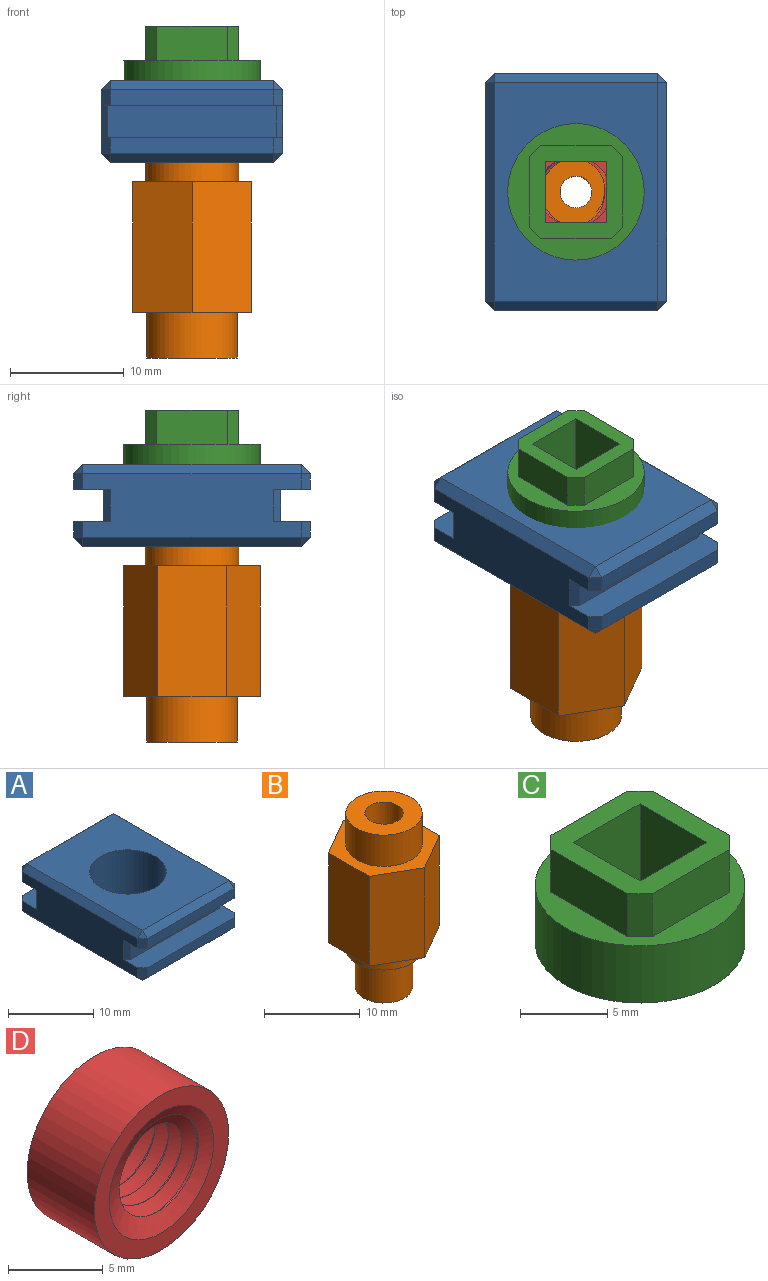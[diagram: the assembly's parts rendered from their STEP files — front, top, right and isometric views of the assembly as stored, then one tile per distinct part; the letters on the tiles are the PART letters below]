
ASSEMBLY  parts=4 mates=3
PART A: 43 faces, bbox 16x20.8x7.2 mm
  f0: plane 14.4x1.4mm, normal (0,-1,0), area 20.2mm2, adj f13,f31,f32,f33
  f1: plane 14.4x1.4mm, normal (0,1,0), area 20.2mm2, adj f11,f36,f39,f42
  f2: plane 19.2x5.6mm, normal (-1,0,0), area 94.1mm2, adj f9,f11,f12,f13,f15,f19,f20,f27
  f3: plane 19.2x5.6mm, normal (1,0,0), area 94.1mm2, adj f9,f11,f12,f13,f17,f23,f26,f29
  f4: plane 14.4x1.4mm, normal (0,-1,0), area 20.2mm2, adj f12,f15,f17,f18
  f5: cylinder r=4.5mm len=9mm, axis (0,0,-1), area 203.6mm2, adj f7,f8
  f6: plane 14.4x1.4mm, normal (0,1,0), area 20.2mm2, adj f9,f20,f24,f26
  f7: plane 19.2x14.4mm, normal (0,0,1), area 212.9mm2, adj f5,f18,f19,f23,f24
  f8: plane 19.2x14.4mm, normal (0,0,-1), area 212.9mm2, adj f5,f32,f37,f38,f42
  f9: plane 16x3.2mm, normal (0,0,-1), area 41.3mm2, adj f2,f3,f6,f10,f20,f26,f28,f29
  f10: plane 14.8x2.8mm, normal (0,1,0), area 41.4mm2, adj f9,f11,f28,f29
  f11: plane 16x3.2mm, normal (0,0,1), area 41.3mm2, adj f1,f2,f3,f10,f28,f29,f36,f39
  f12: plane 16x3.2mm, normal (0,0,-1), area 41.3mm2, adj f2,f3,f4,f14,f15,f17,f27,f30
  f13: plane 16x3.2mm, normal (0,0,1), area 41.3mm2, adj f0,f2,f3,f14,f27,f30,f31,f33
  f14: plane 14.8x2.8mm, normal (0,-1,0), area 41.4mm2, adj f12,f13,f27,f30
  f15: plane 1.4x0.8mm, normal (-0.71,-0.71,0), area 1.6mm2, adj f2,f4,f12,f16
  f16: plane 0.8x0.8mm, normal (-0.58,-0.58,0.58), area 0.6mm2, adj f15,f18,f19
  f17: plane 1.4x0.8mm, normal (0.71,-0.71,0), area 1.6mm2, adj f3,f4,f12,f21
  f18: plane 14.4x0.8mm, normal (0,-0.71,0.71), area 16.3mm2, adj f4,f7,f16,f21
  f19: plane 19.2x0.8mm, normal (-0.71,0,0.71), area 21.7mm2, adj f2,f7,f16,f22
  f20: plane 1.4x0.8mm, normal (-0.71,0.71,0), area 1.6mm2, adj f2,f6,f9,f22
  f21: plane 0.8x0.8mm, normal (0.58,-0.58,0.58), area 0.6mm2, adj f17,f18,f23
  f22: plane 0.8x0.8mm, normal (-0.58,0.58,0.58), area 0.6mm2, adj f19,f20,f24
  f23: plane 19.2x0.8mm, normal (0.71,0,0.71), area 21.7mm2, adj f3,f7,f21,f25
  f24: plane 14.4x0.8mm, normal (0,0.71,0.71), area 16.3mm2, adj f6,f7,f22,f25
  f25: plane 0.8x0.8mm, normal (0.58,0.58,0.58), area 0.6mm2, adj f23,f24,f26
  f26: plane 1.4x0.8mm, normal (0.71,0.71,0), area 1.6mm2, adj f3,f6,f9,f25
  f27: plane 2.8x0.6mm, normal (-0.71,-0.71,0), area 2.4mm2, adj f2,f12,f13,f14
  f28: plane 2.8x0.6mm, normal (-0.71,0.71,0), area 2.4mm2, adj f2,f9,f10,f11
  f29: plane 2.8x0.6mm, normal (0.71,0.71,0), area 2.4mm2, adj f3,f9,f10,f11
  f30: plane 2.8x0.6mm, normal (0.71,-0.71,0), area 2.4mm2, adj f3,f12,f13,f14
  f31: plane 1.4x0.8mm, normal (-0.71,-0.71,0), area 1.6mm2, adj f0,f2,f13,f34
  f32: plane 14.4x0.8mm, normal (0,-0.71,-0.71), area 16.3mm2, adj f0,f8,f34,f35
  f33: plane 1.4x0.8mm, normal (0.71,-0.71,0), area 1.6mm2, adj f0,f3,f13,f35
  f34: plane 0.8x0.8mm, normal (-0.58,-0.58,-0.58), area 0.6mm2, adj f31,f32,f37
  f35: plane 0.8x0.8mm, normal (0.58,-0.58,-0.58), area 0.6mm2, adj f32,f33,f38
  f36: plane 1.4x0.8mm, normal (-0.71,0.71,0), area 1.6mm2, adj f1,f2,f11,f40
  f37: plane 19.2x0.8mm, normal (-0.71,0,-0.71), area 21.7mm2, adj f2,f8,f34,f40
  f38: plane 19.2x0.8mm, normal (0.71,0,-0.71), area 21.7mm2, adj f3,f8,f35,f41
  f39: plane 1.4x0.8mm, normal (0.71,0.71,0), area 1.6mm2, adj f1,f3,f11,f41
  f40: plane 0.8x0.8mm, normal (-0.58,0.58,-0.58), area 0.6mm2, adj f36,f37,f42
  f41: plane 0.8x0.8mm, normal (0.58,0.58,-0.58), area 0.6mm2, adj f38,f39,f42
  f42: plane 14.4x0.8mm, normal (0,0.71,-0.71), area 16.3mm2, adj f1,f8,f40,f41
PART B: 17 faces, bbox 10.4x12x22.2 mm
  f0: plane 4x4mm, normal (0,0,1), area 6.4mm2, adj f1,f14
  f1: cylinder r=1.4mm len=18.2mm, axis (0,0,1), area 160.1mm2, adj f0,f5
  f2: cylinder r=4.1mm len=8.2mm, axis (0,0,1), area 43.8mm2, adj f3,f13
  f3: plane 8.2x8.2mm, normal (0,0,-1), area 24.5mm2, adj f2,f4
  f4: cylinder r=3mm len=6mm, axis (0,0,1), area 94.2mm2, adj f3,f5
  f5: plane 6x6mm, normal (0,0,-1), area 22.1mm2, adj f1,f4
  f6: plane 11.5x6mm, normal (1,0,0), area 69mm2, adj f7,f11,f12,f13
  f7: plane 11.5x5.2mm, normal (0.5,0.87,0), area 69mm2, adj f6,f8,f12,f13
  f8: plane 11.5x5.2mm, normal (-0.5,0.87,0), area 69mm2, adj f7,f9,f12,f13
  f9: plane 11.5x6mm, normal (-1,0,0), area 69mm2, adj f8,f10,f12,f13
  f10: plane 11.5x5.2mm, normal (-0.5,-0.87,0), area 69mm2, adj f9,f11,f12,f13
  f11: plane 11.5x5.2mm, normal (0.5,-0.87,0), area 69mm2, adj f6,f10,f12,f13
  f12: plane 12x10.39mm, normal (0,0,1), area 43.3mm2, adj f6,f7,f8,f9,f10,f11,f15
  f13: plane 12x10.39mm, normal (0,0,-1), area 40.7mm2, adj f2,f6,f7,f8,f9,f10,f11
  f14: cylinder r=2mm len=4mm, axis (0,0,-1), area 50.3mm2, adj f0,f16
  f15: cylinder r=4mm len=8mm, axis (0,0,-1), area 100.5mm2, adj f12,f16
  f16: plane 8x8mm, normal (0,0,1), area 37.7mm2, adj f14,f15
PART C: 16 faces, bbox 12x12x7 mm
  f0: cylinder r=6mm len=12mm, axis (0,0,-1), area 150.8mm2, adj f1,f2
  f1: plane 12x12mm, normal (0,0,1), area 47.9mm2, adj f0,f3,f4,f5,f10,f12,f13,f14
  f2: plane 12x12mm, normal (0,0,-1), area 83.9mm2, adj f0,f6,f7,f8,f9
  f3: plane 6.2x3mm, normal (0,1,0), area 18.6mm2, adj f1,f11,f14,f15
  f4: plane 6.2x3mm, normal (-1,0,0), area 18.6mm2, adj f1,f11,f12,f15
  f5: plane 6.2x3mm, normal (0,-1,0), area 18.6mm2, adj f1,f11,f12,f13
  f6: plane 7x5.4mm, normal (1,0,0), area 37.8mm2, adj f2,f7,f9,f11
  f7: plane 7x5.4mm, normal (0,-1,0), area 37.8mm2, adj f2,f6,f8,f11
  f8: plane 7x5.4mm, normal (-1,0,0), area 37.8mm2, adj f2,f7,f9,f11
  f9: plane 7x5.4mm, normal (0,1,0), area 37.8mm2, adj f2,f6,f8,f11
  f10: plane 6.2x3mm, normal (1,0,0), area 18.6mm2, adj f1,f11,f13,f14
  f11: plane 8.2x8.2mm, normal (0,0,1), area 36.1mm2, adj f3,f4,f5,f6,f7,f8,f9,f10
  f12: plane 3x1mm, normal (-0.71,-0.71,0), area 4.2mm2, adj f1,f4,f5,f11
  f13: plane 3x1mm, normal (0.71,-0.71,0), area 4.2mm2, adj f1,f5,f10,f11
  f14: plane 3x1mm, normal (0.71,0.71,0), area 4.2mm2, adj f1,f3,f10,f11
  f15: plane 3x1mm, normal (-0.71,0.71,0), area 4.2mm2, adj f1,f3,f4,f11
PART D: 8 faces, bbox 10.5x6.1x10.5 mm
  f0: cylinder r=2.5mm len=5mm, axis (0,-1,0), area 0.7mm2, adj f1,f2,f6,f7
  f1: bspline ~7.75x6.71mm, area 66.9mm2, adj f0,f3,f6,f7
  f2: bspline ~7.75x6.71mm, area 66.8mm2, adj f0,f3,f6,f7
  f3: bspline ~6.73x6.73mm, area 20.1mm2, adj f1,f2,f6,f7
  f4: plane 10x10mm, normal (0,-1,0), area 30.9mm2, adj f5,f7
  f5: cylinder r=5mm len=10mm, axis (0,-1,0), area 157.1mm2, adj f4,f6
  f6: plane 10.48x10.48mm, normal (0,1,0), area 51.6mm2, adj f0,f1,f2,f3,f5
  f7: cone r=2.16mm half-angle=66.7deg, axis (0,-1,0), area 22.7mm2, adj f0,f1,f2,f3,f4
PLACE A t=(-4.45,2.43,-1.49)mm
PLACE B rot(axis=(-1,0,0),180deg) t=(-4.45,2.43,-3.19)mm
PLACE C t=(-4.45,2.43,-21.49)mm
PLACE D rot(axis=(1,0,0),90deg) t=(-4.45,2.43,-1.49)mm
MATE fastened B.f2 <-> D.f0  axis (0,0,1) through (-4.45,2.43,-1.49)mm
MATE fastened C.f0 <-> D.f0  axis (0,0,1) through (-4.45,2.43,3.51)mm
MATE fastened D.f0 <-> A.f5  axis (0,0,-1) through (-4.45,2.43,-1.49)mm
